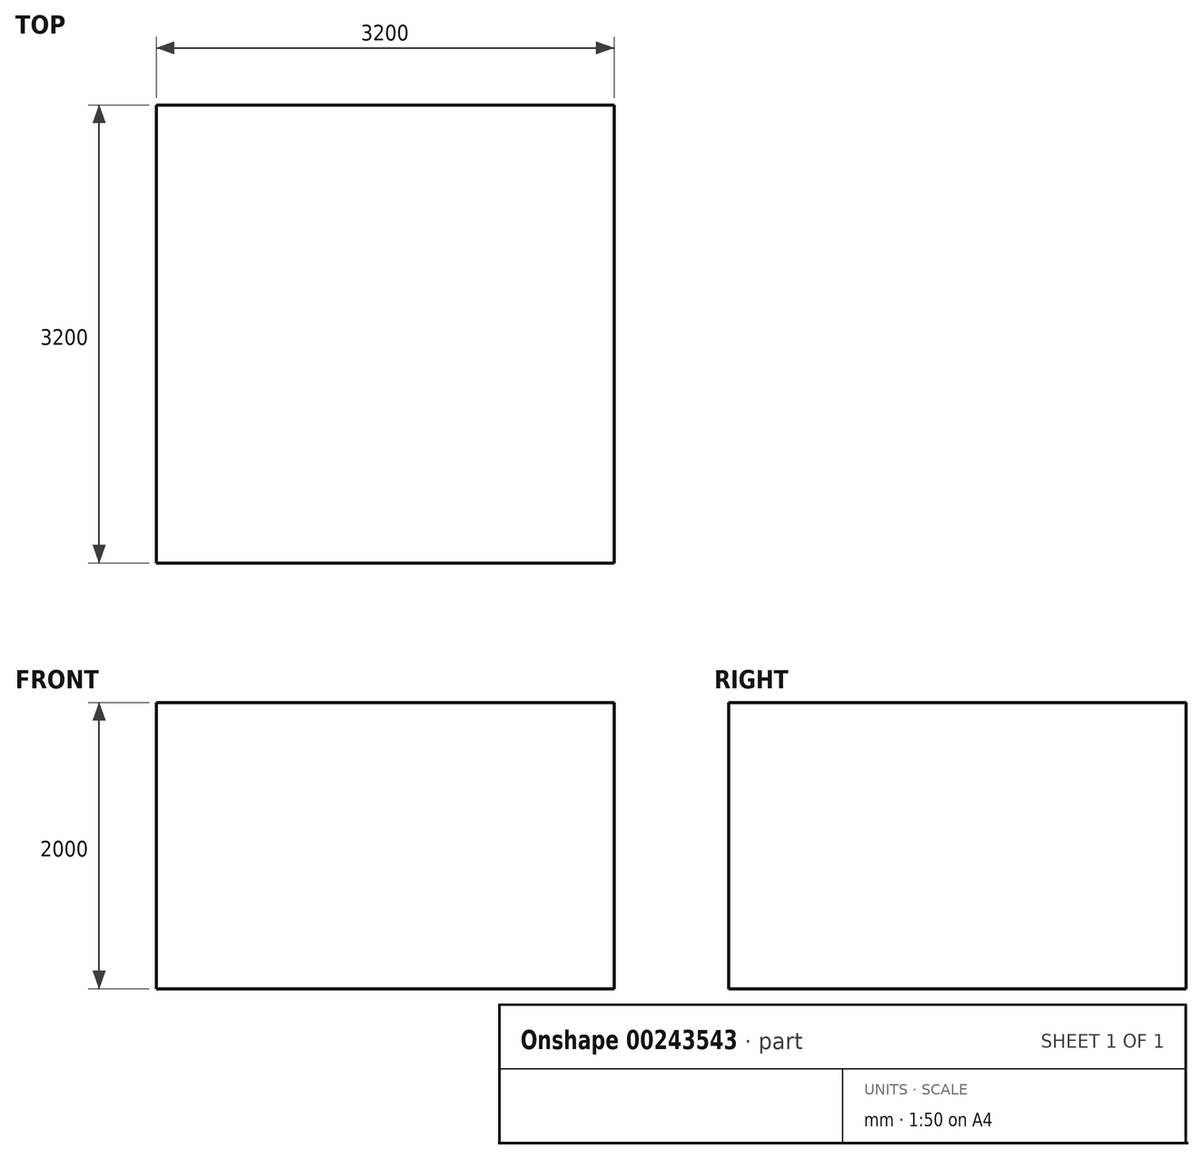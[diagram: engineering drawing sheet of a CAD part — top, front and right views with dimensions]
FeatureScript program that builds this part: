
annotation { "Feature Type Name" : "Feature", "Feature Type Description" : "" }
export const myFeature = defineFeature(function(context is Context, id is Id, definition is map)
    precondition{}
    {
        {
            var Q0;
            Q0=qCreatedBy(makeId("Right.planeOp"),FACE);
            var sketch = newSketch(context, id + "F0", { "sketchPlane" : qUnion([Q0])});
            skLineSegment(sketch, "E0.bottom", {"start": v(-1600, 1000) * mm, "end": v(1600, 1000) * mm});
            skLineSegment(sketch, "E0.top", {"start": v(-1600, -1000) * mm, "end": v(1600, -1000) * mm});
            skLineSegment(sketch, "E0.left", {"start": v(-1600, 1000) * mm, "end": v(-1600, -1000) * mm});
            skLineSegment(sketch, "E0.right", {"start": v(1600, 1000) * mm, "end": v(1600, -1000) * mm});
            skPoint(sketch, "E0.middle", {"position": v(0, 0) * mm});
            skSolve(sketch);
        }
        {
            var Q0;
            Q0=makeQuery(id+"F0.imprint","IMPRINT",FACE,{"disambiguationData":[TD([[makeQuery(id+"F0.imprint","IMPRINT",EDGE,{"derivedFrom":sQuery(id+"F0.wireOp",EDGE,"E0.bottom")}),-1.0]])]});
            extrude(context, id + "F1", {"entities" : qUnion([Q0]), "endBound" : BoundingType.SYMMETRIC, "depth" : 3200 * mm});
        }
    });
